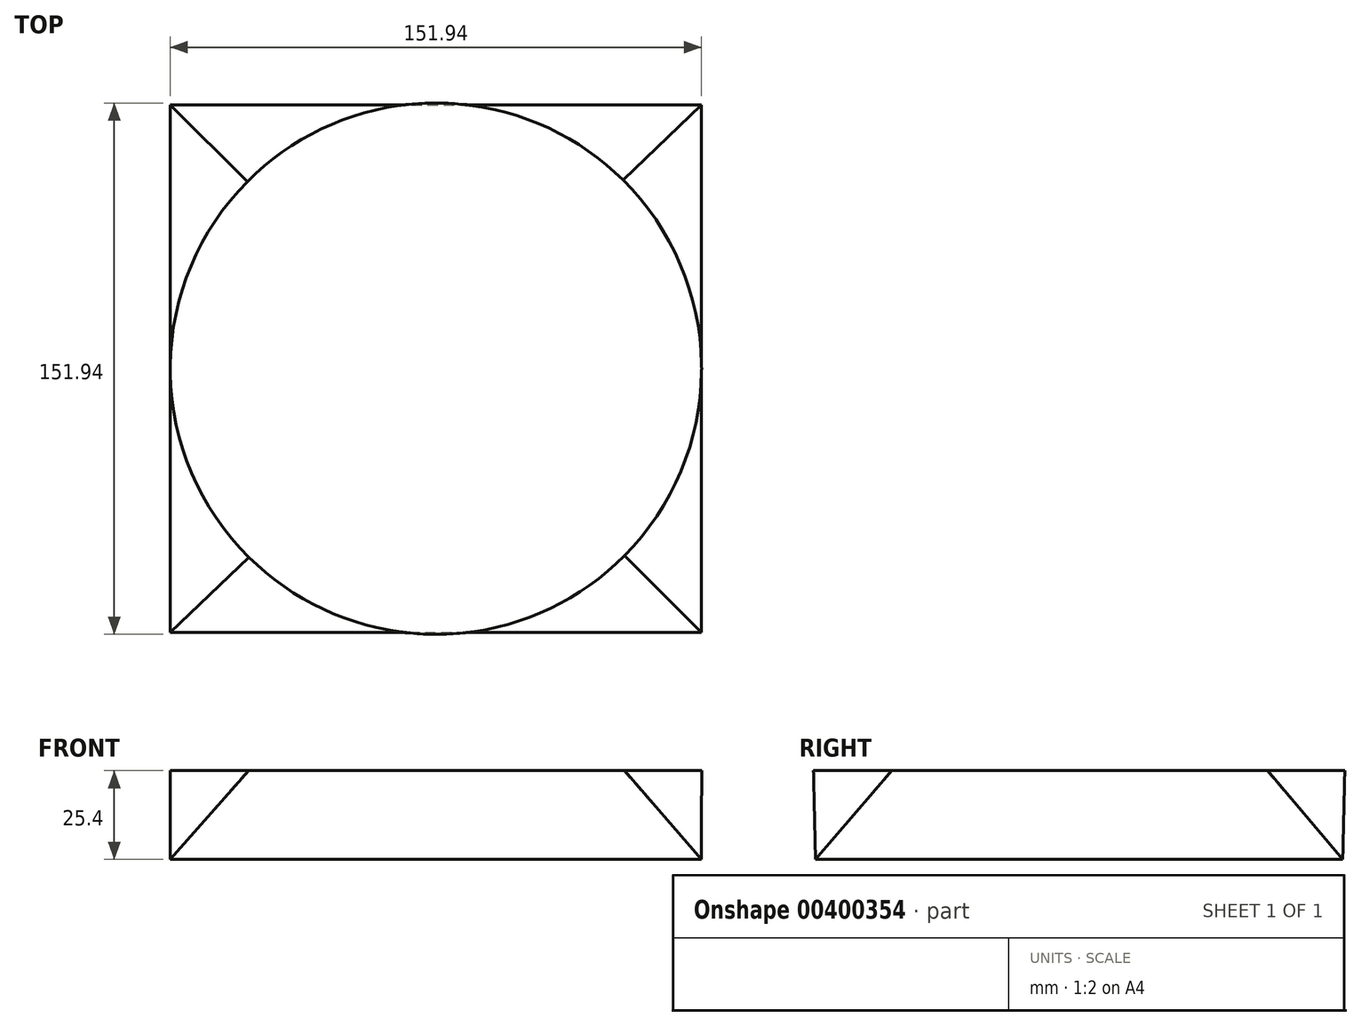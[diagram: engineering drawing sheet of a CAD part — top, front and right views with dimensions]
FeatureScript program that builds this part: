
annotation { "Feature Type Name" : "Feature", "Feature Type Description" : "" }
export const myFeature = defineFeature(function(context is Context, id is Id, definition is map)
    precondition{}
    {
        {
            var Q0;
            Q0=qCreatedBy(makeId("Top.planeOp"),FACE);
            cPlane(context, id + "F0", {"entities" : qUnion([Q0]), "cplaneType" : CPlaneType.OFFSET, "offset" : 25.4 * mm, "width" : 152.4 * mm, "height" : 152.4 * mm});
        }
        {
            var Q0;
            Q0=qCreatedBy(id+"F0.planeOp",FACE);
            var sketch = newSketch(context, id + "F1", { "sketchPlane" : qUnion([Q0])});
            skCircle(sketch, "E0", {"center": v(0, 0) * mm, "radius": 75.97 * mm});
            skSolve(sketch);
        }
        {
            var Q0;
            Q0=qCreatedBy(makeId("Top.planeOp"),FACE);
            var sketch = newSketch(context, id + "F2", { "sketchPlane" : qUnion([Q0])});
            skLineSegment(sketch, "E1.bottom", {"start": v(-75.96, 75.4) * mm, "end": v(75.96, 75.4) * mm});
            skLineSegment(sketch, "E1.top", {"start": v(-75.96, -75.4) * mm, "end": v(75.96, -75.4) * mm});
            skLineSegment(sketch, "E1.left", {"start": v(-75.96, 75.4) * mm, "end": v(-75.96, -75.4) * mm});
            skLineSegment(sketch, "E1.right", {"start": v(75.96, 75.4) * mm, "end": v(75.96, -75.4) * mm});
            skPoint(sketch, "E1.middle", {"position": v(0, 0) * mm});
            skSolve(sketch);
        }
        {
            var Q0;
            Q0 = qSketchRegion(id + "F1", true);
            var Q1;
            Q1 = qSketchRegion(id + "F2", true);
            loft(context, id + "F3", {"sheetProfilesArray" : [{ "sheetProfileEntities" : qUnion([Q0]) }, { "sheetProfileEntities" : qUnion([Q1]) }]});
        }
    });
